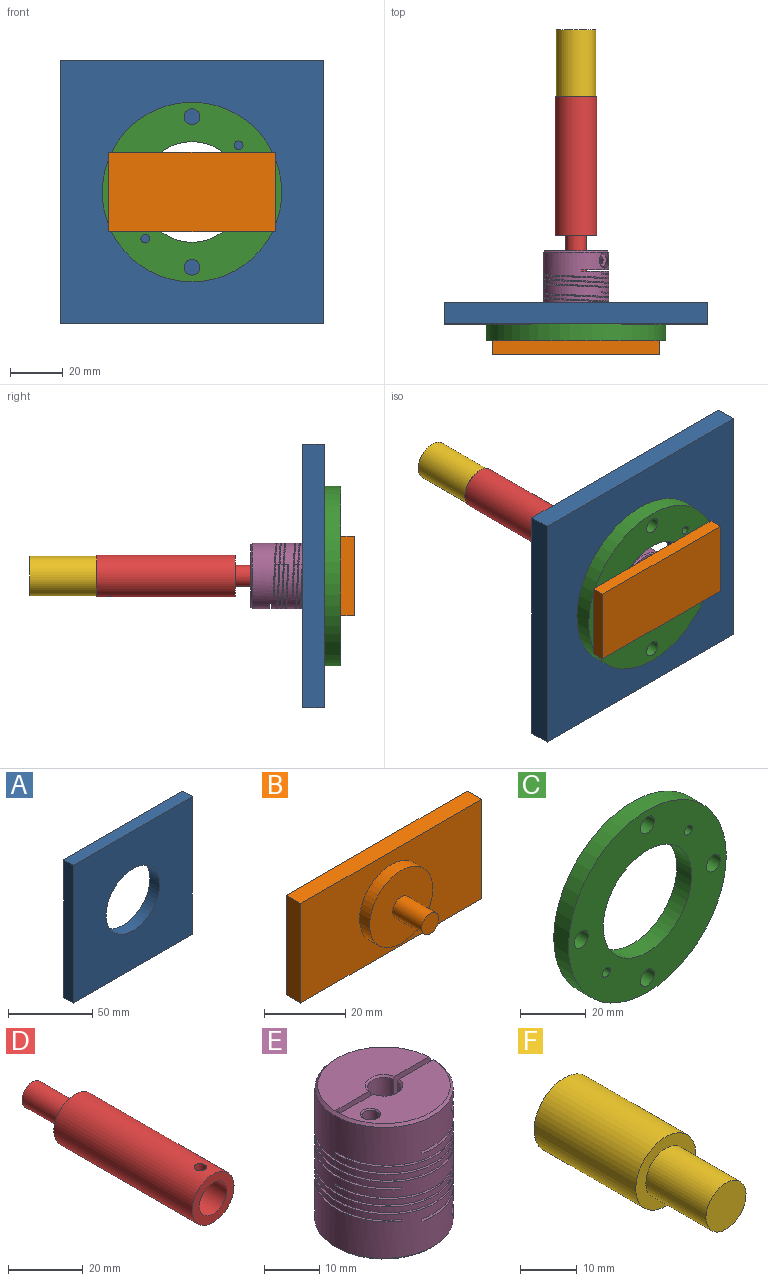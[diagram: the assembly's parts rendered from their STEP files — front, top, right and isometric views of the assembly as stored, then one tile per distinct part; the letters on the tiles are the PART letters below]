
ASSEMBLY  parts=6 mates=9
PART A: 7 faces, bbox 100x8.1x100 mm
  f0: plane 100x8.08mm, normal (-1,0,0), area 807.7mm2, adj f1,f3,f5,f6
  f1: plane 100x8.08mm, normal (0,0,-1), area 807.7mm2, adj f0,f2,f5,f6
  f2: plane 100x8.08mm, normal (1,0,0), area 807.7mm2, adj f1,f3,f5,f6
  f3: plane 100x8.08mm, normal (0,0,1), area 807.7mm2, adj f0,f2,f5,f6
  f4: cylinder r=22.5mm len=45mm, axis (0,1,0), area 1141.9mm2, adj f5,f6
  f5: plane 100x100mm, normal (0,-1,0), area 8409.6mm2, adj f0,f1,f2,f3,f4
  f6: plane 100x100mm, normal (0,1,0), area 8409.6mm2, adj f0,f1,f2,f3,f4
PART B: 10 faces, bbox 63x18.6x30 mm
  f0: plane 30x5mm, normal (-1,0,0), area 150mm2, adj f1,f3,f4,f5
  f1: plane 63x5mm, normal (0,0,-1), area 315mm2, adj f0,f2,f4,f5
  f2: plane 30x5mm, normal (1,0,0), area 150mm2, adj f1,f3,f4,f5
  f3: plane 63x5mm, normal (0,0,1), area 315mm2, adj f0,f2,f4,f5
  f4: plane 63x30mm, normal (0,-1,0), area 1509.9mm2, adj f0,f1,f2,f3,f6
  f5: plane 63x30mm, normal (0,1,0), area 1890mm2, adj f0,f1,f2,f3
  f6: cylinder r=11mm len=22mm, axis (0,1,0), area 241.9mm2, adj f4,f7
  f7: plane 22x22mm, normal (0,-1,0), area 351.9mm2, adj f6,f8
  f8: cylinder r=3mm len=10.1mm, axis (0,1,0), area 190.4mm2, adj f7,f9
  f9: plane 6x6mm, normal (0,-1,0), area 28.3mm2, adj f8
PART C: 10 faces, bbox 68x6.4x68 mm
  f0: cylinder r=3mm len=6.35mm, axis (0,1,0), area 119.7mm2, adj f8,f9
  f1: cylinder r=3mm len=6.35mm, axis (0,1,0), area 119.7mm2, adj f8,f9
  f2: cylinder r=3mm len=6.35mm, axis (0,1,0), area 119.7mm2, adj f8,f9
  f3: cylinder r=3mm len=6.35mm, axis (0,1,0), area 119.7mm2, adj f8,f9
  f4: cylinder r=19.05mm len=38.1mm, axis (0,1,0), area 760.1mm2, adj f8,f9
  f5: cylinder r=1.65mm len=6.35mm, axis (0,1,0), area 65.8mm2, adj f8,f9
  f6: cylinder r=1.65mm len=6.35mm, axis (0,1,0), area 65.8mm2, adj f8,f9
  f7: cylinder r=34mm len=68mm, axis (0,1,0), area 1356.5mm2, adj f8,f9
  f8: plane 68x68mm, normal (0,-1,0), area 2361.4mm2, adj f0,f1,f2,f3,f4,f5,f6,f7
  f9: plane 68x68mm, normal (0,1,0), area 2361.4mm2, adj f0,f1,f2,f3,f4,f5,f6,f7
PART D: 8 faces, bbox 15.9x68.4x15.9 mm
  f0: cylinder r=7.94mm len=52.39mm, axis (0,1,0), area 2604.1mm2, adj f2,f3,f7
  f1: cylinder r=5.16mm len=25.4mm, axis (0,-1,0), area 814.8mm2, adj f2,f4,f7
  f2: plane 15.88x15.88mm, normal (0,-1,0), area 114.3mm2, adj f0,f1
  f3: plane 15.88x15.88mm, normal (0,1,0), area 147.7mm2, adj f0,f5
  f4: plane 10.32x10.32mm, normal (0,-1,0), area 83.6mm2, adj f1
  f5: cylinder r=4mm len=16mm, axis (0,-1,0), area 402.1mm2, adj f3,f6
  f6: plane 8x8mm, normal (0,1,0), area 50.3mm2, adj f5
  f7: cylinder r=1.65mm len=3.3mm, axis (0,0,-1), area 29.3mm2, adj f0,f1
PART E: 93 faces, bbox 25.3x25.3x30 mm
  f0: plane 0.38x0.38mm, normal (0,0,-1), area 0.1mm2, adj f1
  f1: cone r=0mm half-angle=67.5deg, axis (0,0,-1), area 8.4mm2, adj f0,f2
  f2: cylinder r=1.59mm len=5.52mm, axis (0,0,-1), area 55mm2, adj f1,f3
  f3: cone r=0mm half-angle=45deg, axis (0,0,-1), area 3.9mm2, adj f2,f11
  f4: plane 7.75x5.83mm, normal (0,-1,0), area 26.6mm2, adj f5,f11,f12,f14
  f5: cylinder r=19.05mm len=7.75mm, axis (0,1,0), area 11.7mm2, adj f4,f6,f11,f14
  f6: plane 7.75x5.83mm, normal (0,1,0), area 26.6mm2, adj f5,f7,f11,f14
  f7: cone r=0mm half-angle=45deg, axis (0,0,-1), area 6.4mm2, adj f6,f11,f14,f19
  f8: cone r=0mm half-angle=30deg, axis (0,1,0), area 7.1mm2, adj f15,f16,f19
  f9: plane 0.38x0.38mm, normal (0,0,1), area 0.1mm2, adj f20
  f10: plane 5.95x5.95mm, normal (0,1,0), area 19.5mm2, adj f13,f21,f22
  f11: plane 23.98x23.96mm, normal (0,0,-1), area 362.7mm2, adj f3,f4,f5,f6,f7,f12,f19,f23
  f12: cone r=0mm half-angle=45deg, axis (0,0,-1), area 6.4mm2, adj f4,f11,f14,f24
  f13: cylinder r=1.63mm len=3.26mm, axis (0,-1,0), area 26.4mm2, adj f10,f24
  f14: cylinder r=4mm len=8mm, axis (0,0,1), area 163.5mm2, adj f4,f5,f6,f7,f12,f17,f18,f19
  f15: cylinder r=1.29mm len=8.24mm, axis (0,1,0), area 33.4mm2, adj f8,f16,f35
  f16: cylinder r=1.29mm len=8.24mm, axis (0,1,0), area 33.4mm2, adj f8,f15,f35
  f17: plane 9.15x0.64mm, normal (1,0,0), area 5.8mm2, adj f14,f18,f27,f35
  f18: plane 15.02x11.9mm, normal (0,0,1), area 127.1mm2, adj f14,f17,f19,f35
  f19: plane 8.53x7.17mm, normal (0,1,0), area 52.1mm2, adj f7,f8,f11,f14,f18,f23,f35
  f20: cone r=0mm half-angle=67.5deg, axis (0,0,1), area 8.4mm2, adj f9,f33
  f21: cylinder r=2.98mm len=6.32mm, axis (0,-1,0), area 38.7mm2, adj f10,f22,f35
  f22: cylinder r=2.98mm len=6.32mm, axis (0,-1,0), area 59.1mm2, adj f10,f21,f35
  f23: cone r=0mm half-angle=45deg, axis (0,0,1), area 54.4mm2, adj f11,f19,f24,f35
  f24: plane 8.53x7.17mm, normal (0,-1,0), area 52.5mm2, adj f11,f12,f13,f14,f23,f25,f35
  f25: plane 15.02x11.9mm, normal (0,0,1), area 127.1mm2, adj f14,f24,f26,f35
  f26: plane 9.15x0.64mm, normal (1,0,0), area 5.8mm2, adj f14,f25,f27,f35
  f27: plane 24.99x15.04mm, normal (0,0,-1), area 264.4mm2, adj f14,f17,f26,f35
  f28: plane 8.89x8.89mm, normal (0,0,1), area 11.8mm2, adj f14,f37
  f29: cylinder r=12.5mm len=24.99mm, axis (0,0,-1), area 49.6mm2, adj f32,f35,f40,f42
  f30: plane 6.96x4.06mm, normal (-0.86,0.5,0), area 3.3mm2, adj f35,f37,f39,f42
  f31: cylinder r=4.45mm len=8.89mm, axis (0,0,1), area 17.6mm2, adj f32,f37,f41,f42
  f32: bspline ~25.31x25.2mm, area 715.5mm2, adj f29,f31,f35,f36,f37,f40,f41,f43
  f33: cylinder r=1.59mm len=5.52mm, axis (0,0,1), area 55mm2, adj f20,f47
  f34: cylinder r=12.5mm len=24.99mm, axis (0,0,-1), area 49.6mm2, adj f35,f39,f48,f49
  f35: cylinder r=12.5mm len=24.99mm, axis (0,0,-1), area 639.2mm2, adj f15,f16,f17,f18,f19,f21,f22,f23
  f36: plane 6.96x4.06mm, normal (0.86,-0.5,0), area 3.3mm2, adj f32,f35,f37,f49
  f37: cylinder r=4.45mm len=8.89mm, axis (0,0,1), area 49.2mm2, adj f28,f30,f31,f32,f36,f38,f39,f42
  f38: cylinder r=4.45mm len=8.89mm, axis (0,0,1), area 17.6mm2, adj f37,f39,f49,f51
  f39: bspline ~25.31x25.2mm, area 715.5mm2, adj f30,f34,f35,f37,f38,f48,f50,f51
  f40: cylinder r=12.5mm len=24.99mm, axis (0,0,-1), area 49.6mm2, adj f29,f32,f42,f67
  f41: cylinder r=4.45mm len=8.89mm, axis (0,0,1), area 17.6mm2, adj f31,f32,f42,f69
  f42: bspline ~24.99x24.98mm, area 715.5mm2, adj f29,f30,f31,f35,f37,f40,f41,f50
  f43: plane 8.05x0.41mm, normal (0,-1,0), area 3.3mm2, adj f32,f49,f67,f69
  f44: plane 8.77x6.21mm, normal (0,1,0), area 32.7mm2, adj f45,f57,f61,f64
  f45: cylinder r=19.05mm len=8.76mm, axis (0,1,0), area 13mm2, adj f44,f46,f61,f64
  f46: plane 8.77x6.21mm, normal (0,-1,0), area 32.7mm2, adj f45,f61,f62,f64
  f47: cone r=0mm half-angle=45deg, axis (0,0,1), area 3.9mm2, adj f33,f64
  f48: cylinder r=12.5mm len=24.99mm, axis (0,0,-1), area 49.6mm2, adj f34,f39,f49,f67
  f49: bspline ~24.99x24.98mm, area 715.5mm2, adj f34,f35,f36,f37,f38,f43,f48,f51
  f50: plane 8.05x0.41mm, normal (0,1,0), area 3.3mm2, adj f39,f42,f67,f69
  f51: cylinder r=4.45mm len=8.89mm, axis (0,0,1), area 17.6mm2, adj f38,f39,f49,f69
  f52: bspline ~24.99x24.98mm, area 715.5mm2, adj f53,f55,f56,f67,f68,f69,f75,f76
  f53: cylinder r=12.5mm len=24.99mm, axis (0,0,-1), area 49.6mm2, adj f52,f67,f76,f77
  f54: plane 6.96x4.06mm, normal (0.86,-0.5,0), area 3.3mm2, adj f65,f67,f69,f77
  f55: cylinder r=4.45mm len=8.89mm, axis (0,0,1), area 17.6mm2, adj f52,f56,f69,f77
  f56: cylinder r=4.45mm len=8.89mm, axis (0,0,1), area 17.6mm2, adj f52,f55,f72,f77
  f57: cone r=0mm half-angle=45deg, axis (0,0,1), area 4.8mm2, adj f44,f61,f64,f78
  f58: cone r=0mm half-angle=30deg, axis (0,1,0), area 7.1mm2, adj f73,f74,f78
  f59: plane 8.89x8.89mm, normal (0,0,-1), area 33.8mm2, adj f72,f81
  f60: plane 5.95x5.95mm, normal (0,1,0), area 19.5mm2, adj f63,f82,f83
  f61: cylinder r=3mm len=6.78mm, axis (0,0,-1), area 112.7mm2, adj f44,f45,f46,f57,f62,f78,f85,f86
  f62: cone r=0mm half-angle=45deg, axis (0,0,1), area 4.8mm2, adj f46,f61,f64,f86
  f63: cylinder r=1.63mm len=3.26mm, axis (0,-1,0), area 26.4mm2, adj f60,f86
  f64: plane 23.98x23.96mm, normal (0,0,1), area 384.7mm2, adj f44,f45,f46,f47,f57,f62,f78,f86
  f65: bspline ~24.99x24.98mm, area 715.5mm2, adj f54,f66,f67,f69,f70,f71,f88,f89
  f66: cylinder r=12.5mm len=24.99mm, axis (0,0,-1), area 49.6mm2, adj f65,f67,f89,f90
  f67: cylinder r=12.5mm len=24.99mm, axis (0,0,-1), area 257.2mm2, adj f40,f42,f43,f48,f49,f50,f52,f53
  f68: plane 6.96x4.06mm, normal (-0.86,0.5,0), area 3.3mm2, adj f52,f67,f69,f90
  f69: cylinder r=4.45mm len=8.89mm, axis (0,0,1), area 91.7mm2, adj f41,f42,f43,f49,f50,f51,f52,f54
  f70: cylinder r=4.45mm len=8.89mm, axis (0,0,1), area 17.6mm2, adj f65,f69,f71,f90
  f71: cylinder r=4.45mm len=8.89mm, axis (0,0,1), area 17.6mm2, adj f65,f70,f72,f90
  f72: cylinder r=4.45mm len=8.89mm, axis (0,0,1), area 37.5mm2, adj f56,f59,f71,f75,f77,f88,f90
  f73: cylinder r=1.29mm len=8.24mm, axis (0,1,0), area 33.4mm2, adj f58,f74,f92
  f74: cylinder r=1.29mm len=8.24mm, axis (0,1,0), area 33.4mm2, adj f58,f73,f92
  f75: plane 8.05x0.41mm, normal (0,1,0), area 3.3mm2, adj f52,f72,f90,f92
  f76: cylinder r=12.5mm len=24.99mm, axis (0,0,-1), area 49.6mm2, adj f52,f53,f77,f92
  f77: bspline ~24.99x24.98mm, area 715.5mm2, adj f53,f54,f55,f56,f67,f69,f72,f76
  f78: plane 9.55x7.17mm, normal (0,1,0), area 59.4mm2, adj f57,f58,f61,f64,f85,f87,f92
  f79: plane 9.15x0.64mm, normal (1,0,0), area 5.8mm2, adj f80,f85,f91,f92
  f80: cylinder r=4mm len=6.18mm, axis (0,0,1), area 4.5mm2, adj f79,f84,f85,f91
  f81: cylinder r=3mm len=6mm, axis (0,0,-1), area 2.4mm2, adj f59,f91
  f82: cylinder r=2.98mm len=6.32mm, axis (0,-1,0), area 38.7mm2, adj f60,f83,f92
  f83: cylinder r=2.98mm len=6.32mm, axis (0,-1,0), area 59.1mm2, adj f60,f82,f92
  f84: plane 9.15x0.64mm, normal (1,0,0), area 5.8mm2, adj f80,f85,f91,f92
  f85: plane 24.99x16.48mm, normal (0,0,-1), area 275mm2, adj f61,f78,f79,f80,f84,f86,f92
  f86: plane 9.55x7.17mm, normal (0,-1,0), area 59.8mm2, adj f61,f62,f63,f64,f85,f87,f92
  f87: cone r=0mm half-angle=45deg, axis (0,0,-1), area 54.4mm2, adj f64,f78,f86,f92
  f88: plane 8.05x0.41mm, normal (0,-1,0), area 3.3mm2, adj f65,f72,f77,f92
  f89: cylinder r=12.5mm len=24.99mm, axis (0,0,-1), area 49.6mm2, adj f65,f66,f90,f92
  f90: bspline ~24.99x24.98mm, area 715.5mm2, adj f66,f67,f68,f69,f70,f71,f72,f75
  f91: plane 24.99x16.5mm, normal (0,0,1), area 286.4mm2, adj f79,f80,f81,f84,f92
  f92: cylinder r=12.5mm len=24.99mm, axis (0,0,-1), area 604.9mm2, adj f73,f74,f75,f76,f77,f78,f79,f82
PART F: 5 faces, bbox 15x40.4x15 mm
  f0: cylinder r=7.5mm len=25.4mm, axis (0,1,0), area 1196.9mm2, adj f1,f2
  f1: plane 15x15mm, normal (0,-1,0), area 98.2mm2, adj f0,f3
  f2: plane 15x15mm, normal (0,1,0), area 176.7mm2, adj f0
  f3: cylinder r=5mm len=15mm, axis (0,1,0), area 471.2mm2, adj f1,f4
  f4: plane 10x10mm, normal (0,-1,0), area 78.5mm2, adj f3
PLACE A at identity fixed
PLACE B rot(axis=(1,0,0),180deg) t=(18.5,-19.43,65)mm
PLACE C t=(50,-8.08,50)mm
PLACE D rot(axis=(1,0,0),180deg) t=(50,25.61,50)mm
PLACE E rot(axis=(0.97,0.18,-0.18),91.9deg) t=(50,-2.35,50)mm
PLACE F rot(axis=(0,-1,0),90deg) t=(50,103.4,50)mm
MATE cylindrical E.f7 <-> B.f6  axis (0,1,0) through (50,-6.5,50)mm
MATE cylindrical A.f4 <-> C.f4  axis (0,1,0) through (50,-4.04,50)mm
MATE fastened A.f4 <-> C.f7  axis (0,-1,0) through (50,-8.08,50)mm
MATE fastened F.f0 <-> D.f0  axis (0,-1,0) through (50,78,50)mm
MATE fastened C.f7 <-> B.f6  axis (0,-1,0) through (50,-14.43,50)mm
MATE fastened A.f4 <-> F.f3  axis (0,1,0) through (50,0,50)mm
MATE cylindrical A.f4 <-> F.f0  axis (0,1,0) through (50,-8.08,50)mm
MATE cylindrical A.f4 <-> B.f6  axis (0,1,0) through (50,-8.08,50)mm
MATE cylindrical F.f3 <-> D.f1  axis (0,1,0) through (50,70.5,50)mm
